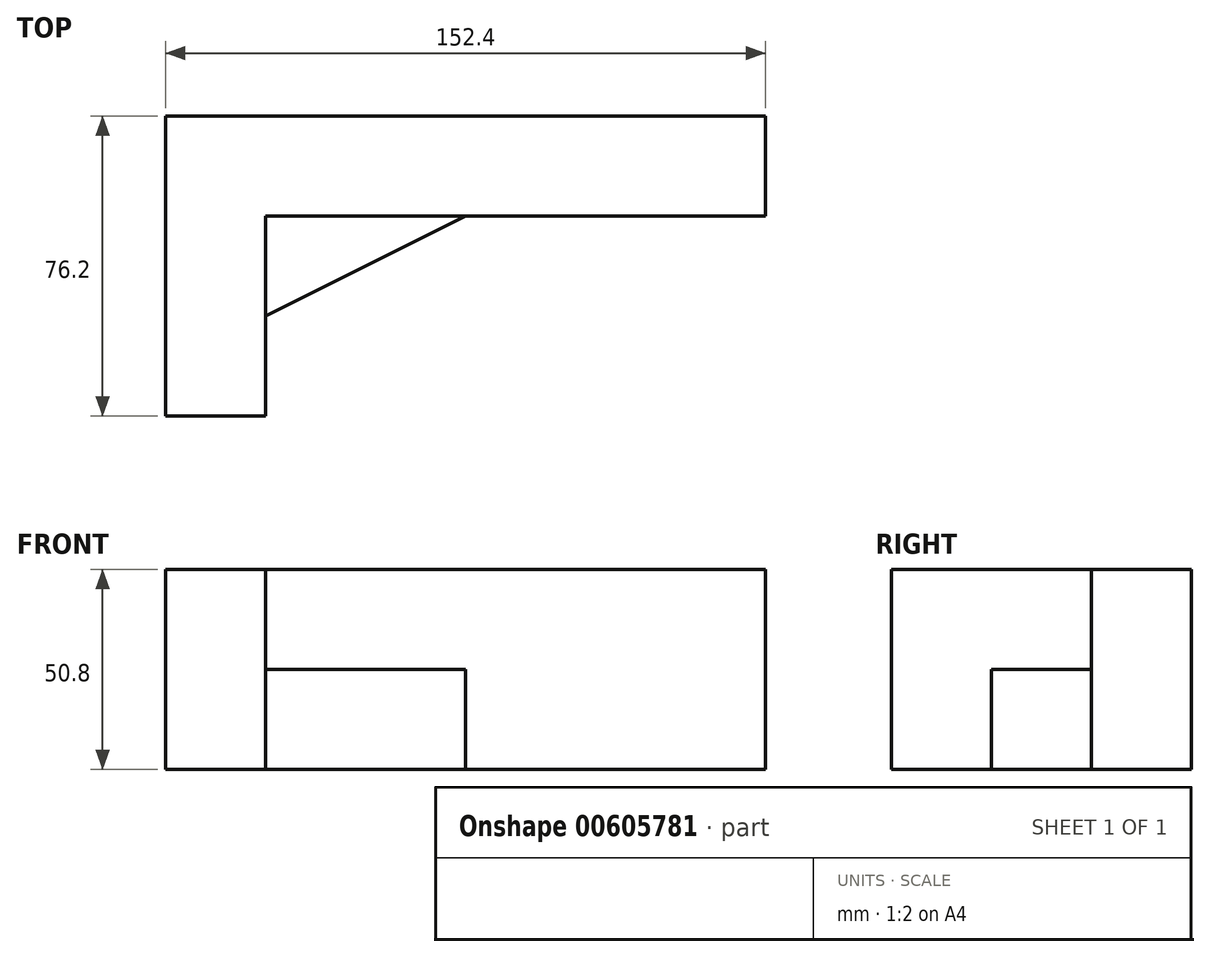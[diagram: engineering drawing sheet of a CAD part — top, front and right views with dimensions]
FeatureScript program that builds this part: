
annotation { "Feature Type Name" : "Feature", "Feature Type Description" : "" }
export const myFeature = defineFeature(function(context is Context, id is Id, definition is map)
    precondition{}
    {
        {
            var Q0;
            Q0=qCreatedBy(makeId("Front.planeOp"),FACE);
            var sketch = newSketch(context, id + "F0", { "sketchPlane" : qUnion([Q0])});
            skLineSegment(sketch, "E0", {"start": v(0, 0) * mm, "end": v(152.4, 0) * mm});
            skLineSegment(sketch, "E1", {"start": v(152.4, 0) * mm, "end": v(152.4, 50.8) * mm});
            skLineSegment(sketch, "E2", {"start": v(152.4, 50.8) * mm, "end": v(0, 50.8) * mm});
            skLineSegment(sketch, "E3", {"start": v(0, 50.8) * mm, "end": v(0, 0) * mm});
            skSolve(sketch);
        }
        {
            var Q0;
            Q0 = qSketchRegion(id + "F0", true);
            extrude(context, id + "F1", {"entities" : qUnion([Q0]), "depth" : 76.2 * mm, "offsetDistance" : 25.4 * mm});
        }
        {
            var Q0;
            Q0=makeQuery(id+"F1.opExtrude","CAP_FACE",FACE,{"disambiguationData":[OSD([sQuery(id+"F0.wireOp",EDGE,"E0"),sQuery(id+"F0.wireOp",EDGE,"E1"),sQuery(id+"F0.wireOp",EDGE,"E2"),sQuery(id+"F0.wireOp",EDGE,"E3")])],"isStart":false});
            var sketch = newSketch(context, id + "F2", { "sketchPlane" : qUnion([Q0])});
            skLineSegment(sketch, "E4", {"start": v(0, 0) * mm, "end": v(25.4, 0) * mm});
            skLineSegment(sketch, "E5", {"start": v(25.4, 0) * mm, "end": v(25.4, 50.8) * mm});
            skLineSegment(sketch, "E6", {"start": v(25.4, 50.8) * mm, "end": v(0, 50.8) * mm});
            skLineSegment(sketch, "E7", {"start": v(25.4, 25.4) * mm, "end": v(76.2, 25.4) * mm});
            skPoint(sketch, "E7.endSnap0", {"position": v(25.4, 25.4) * mm});
            skLineSegment(sketch, "E8", {"start": v(76.2, 25.4) * mm, "end": v(76.2, 0) * mm});
            skLineSegment(sketch, "E9", {"start": v(76.2, 25.4) * mm, "end": v(76.2, 50.8) * mm});
            skLineSegment(sketch, "E10", {"start": v(76.2, 50.8) * mm, "end": v(25.4, 50.8) * mm});
            skLineSegment(sketch, "E11", {"start": v(25.4, 50.8) * mm, "end": v(25.4, 25.4) * mm});
            skSolve(sketch);
        }
        {
            var Q0;
            Q0=makeQuery(id+"F2.imprint","IMPRINT",FACE,{"disambiguationData":[TD([[makeQuery(id+"F2.imprint","IMPRINT",EDGE,{"derivedFrom":sQuery(id+"F2.wireOp",EDGE,"E7")}),1.0]])]});
            extrude(context, id + "F3", {"entities" : qUnion([Q0]), "operationType" : NewBodyOperationType.REMOVE, "oppositeDirection" : true, "depth" : 50.8 * mm, "offsetDistance" : 25.4 * mm});
        }
        {
            var Q0;
            Q0=makeQuery(id+"F1.opExtrude","CAP_FACE",FACE,{"disambiguationData":[OSD([sQuery(id+"F0.wireOp",EDGE,"E0"),sQuery(id+"F0.wireOp",EDGE,"E1"),sQuery(id+"F0.wireOp",EDGE,"E2"),sQuery(id+"F0.wireOp",EDGE,"E3")])],"isStart":false});
            var sketch = newSketch(context, id + "F4", { "sketchPlane" : qUnion([Q0])});
            skLineSegment(sketch, "E12", {"start": v(76.2, 0) * mm, "end": v(76.2, 50.8) * mm});
            skLineSegment(sketch, "E13", {"start": v(76.2, 50.8) * mm, "end": v(152.4, 50.8) * mm});
            skLineSegment(sketch, "E14", {"start": v(152.4, 50.8) * mm, "end": v(152.4, 0) * mm});
            skLineSegment(sketch, "E15", {"start": v(152.4, 0) * mm, "end": v(76.2, 0) * mm});
            skSolve(sketch);
        }
        {
            var Q0;
            Q0 = qSketchRegion(id + "F4", true);
            extrude(context, id + "F5", {"entities" : qUnion([Q0]), "operationType" : NewBodyOperationType.REMOVE, "oppositeDirection" : true, "depth" : 50.8 * mm, "offsetDistance" : 25.4 * mm});
        }
        {
            var Q0;
            Q0=makeQuery(id+"F1.opExtrude","CAP_FACE",FACE,{"disambiguationData":[OSD([sQuery(id+"F0.wireOp",EDGE,"E0"),sQuery(id+"F0.wireOp",EDGE,"E1"),sQuery(id+"F0.wireOp",EDGE,"E2"),sQuery(id+"F0.wireOp",EDGE,"E3")])],"isStart":false});
            var sketch = newSketch(context, id + "F6", { "sketchPlane" : qUnion([Q0])});
            skLineSegment(sketch, "E16", {"start": v(25.4, 25.4) * mm, "end": v(25.4, 0) * mm});
            skLineSegment(sketch, "E17", {"start": v(25.4, 0) * mm, "end": v(76.2, 0) * mm});
            skLineSegment(sketch, "E18", {"start": v(76.2, 0) * mm, "end": v(76.2, 25.4) * mm});
            skLineSegment(sketch, "E19", {"start": v(76.2, 25.4) * mm, "end": v(25.4, 25.4) * mm});
            skSolve(sketch);
        }
        {
            var Q0;
            Q0 = qSketchRegion(id + "F6", true);
            extrude(context, id + "F7", {"entities" : qUnion([Q0]), "operationType" : NewBodyOperationType.REMOVE, "oppositeDirection" : true, "depth" : 25.4 * mm, "offsetDistance" : 25.4 * mm});
        }
        {
            var Q0;
            Q0=makeQuery(id+"F3.boolean.opBoolean","COPY",FACE,{"derivedFrom":makeQuery(id+"F3.opExtrude","SWEPT_FACE",FACE,{"disambiguationData":[OSD([sQuery(id+"F2.wireOp",EDGE,"E7")])]})});
            var sketch = newSketch(context, id + "F8", { "sketchPlane" : qUnion([Q0])});
            skLineSegment(sketch, "E20", {"start": v(25.4, -50.8) * mm, "end": v(76.2, -25.4) * mm});
            skLineSegment(sketch, "E21", {"start": v(76.2, -25.4) * mm, "end": v(76.2, -50.8) * mm});
            skLineSegment(sketch, "E22", {"start": v(76.2, -50.8) * mm, "end": v(25.4, -50.8) * mm});
            skSolve(sketch);
        }
        {
            var Q0;
            Q0=makeQuery(id+"F8.imprint","IMPRINT",FACE,{"disambiguationData":[TD([[makeQuery(id+"F8.imprint","IMPRINT",EDGE,{"derivedFrom":sQuery(id+"F8.wireOp",EDGE,"E20")}),-1.0]])]});
            extrude(context, id + "F9", {"entities" : qUnion([Q0]), "operationType" : NewBodyOperationType.REMOVE, "oppositeDirection" : true, "depth" : 25.4 * mm, "offsetDistance" : 25.4 * mm});
        }
    });
